# Revit family: Electronics_Desono_Biamp_Two-Way-High-Efficiency-Loudspeaker_DX-IC6LP
name_source: partatom
category: Communication Devices
units: mm (PartAtom-declared; Revit-internal decimal feet)

## family parameters
Cut with Voids When Loaded = No
Host = Face
Maintain Annotation Orientation = No
OmniClass Number = 23.85.10.11.14.14.14
OmniClass Title = Loudspeakers
Part Type = Normal
Room Calculation Point = No
Round Connector Dimension = Use Diameter
Shared = No

## types (1)
- DX-IC6LP
    Amplifers = 70 V: 60 W, 30 W, 15 W, 7.5 W, 3.75 W ; 100 V: 60 W, 30 W, 15 W, 7.5 W
    Certifcations = ETL listed to comply with UL1480A, UL2043 and CSA62368-1 Suitable for use in air handling spaces per NFPA 70 and NFPA 90
    Connector Description = 4-way Euroblock; Low impedance 8 ohms, 70/100V operation
    Controls = Front-face wattage / low impedance selector switch
    Crossover Frequency = 2.5 kHz
    Default Elevation = 48 "
    Depth = 4 "
    Description = Desono™ DX-IC6LP Two-Way 6.5-Inch High Efficiency Ceiling Mount Loudspeaker
    Diameter = 13 "
    Grill Material = Biamp - Plastic - White(Grid)
    Housing Material = Biamp - Metal - Black
    Input Connection = 4-position Euroblock connector
    Manufacturer = Biamp
    Model = DX-IC6LP
    Mounting Provisions = 3 SpringLock™ mounting clamps with 33 mm (1.3) grip range
    Nominal Beamwidth  (H x V) = 145°, conical
    Nominal Continuous Power Handling = 22 V (60 W @ 8 Ω)
    Nominal Maximum SPL = Peak - 109dB; Continuous -103dB
    Operating Environment = Indoor
    Operating Mode = Passive with DSP
    Operating Range (-10dB) = 63 Hz to 20 kHz
    Product Documentation Link = https://downloads.biamp.com
    Product Page URL = https://www.biamp.com
    Product data url = https://bimobject.com
    Rated Continuous Voltage = 21.9 V (27 dBV)
    Rated Maximum SPL (Processed) = Peak - 115dB; Continuous -103dB
    Recommended Amplifers = 60 W - 120 W into 8 Ω, (22 V - 31 V)
    Required Accessory = 65 Hz, 18 dB/oct. high pass flter; DSP preset for ALC or Tesira
    Sensitivity = 87 dB (2.83 V); 87 dB (1 W at rated impedance 8 Ω)
    Shipping Weight = 30.42 lb
    Transducers = LF 1 x 6.5 (165 mm) treated paper cone HF 1 x 1.0 (25 mm) treated soft dome driver with waveguide
    URL = https://www.biamp.com
    Version = 1
    Weight = 10.80 lb

## geometry (parser evidence)
native form markers: Sweep x4
no freeform markers — native parametric forms only
